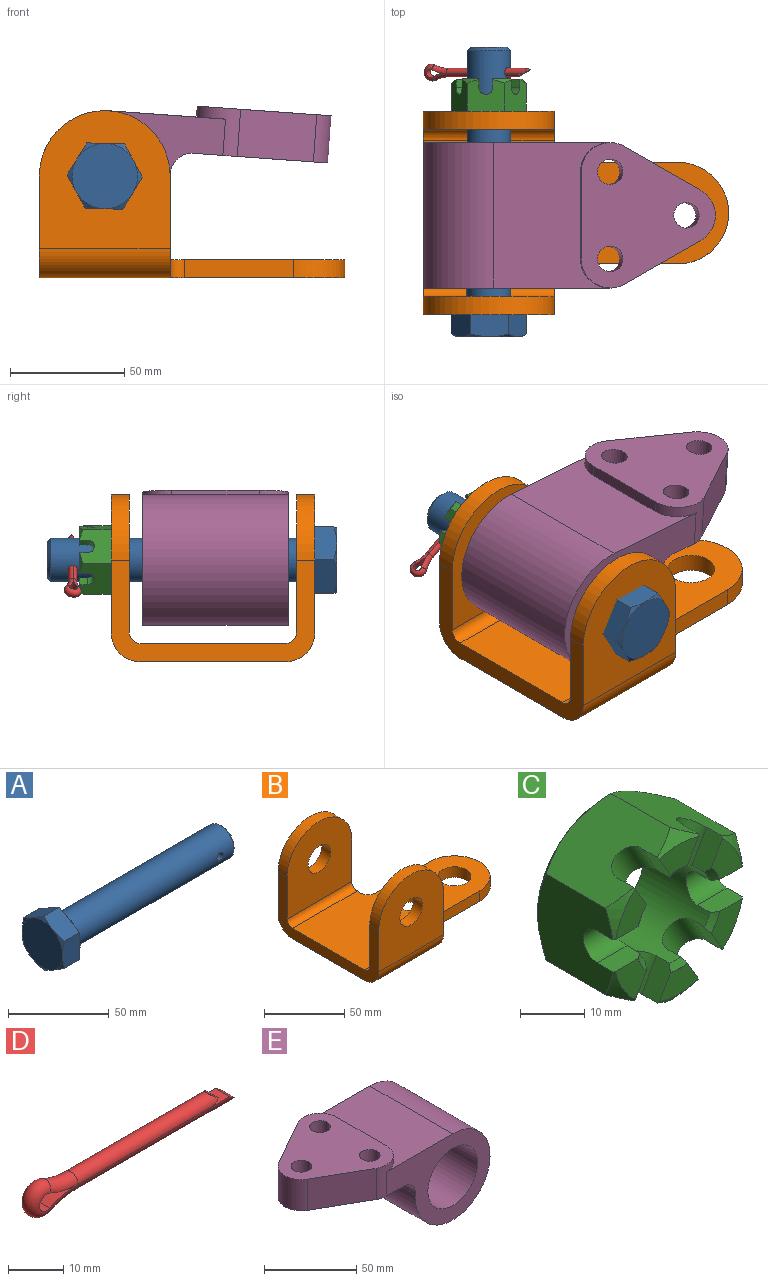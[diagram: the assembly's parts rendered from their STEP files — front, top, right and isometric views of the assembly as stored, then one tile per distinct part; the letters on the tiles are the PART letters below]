
ASSEMBLY  parts=5 mates=4
PART A: 26 faces, bbox 126.6x33x33 mm
  f0: plane 28.58x28.58mm, normal (1,0,0), area 325.1mm2, adj f10,f24
  f1: cylinder r=9.53mm len=112.28mm, axis (-1,0,0), area 6683.8mm2, adj f2,f24,f25
  f2: cone r=8.01mm half-angle=45deg, axis (-1,0,0), area 117.9mm2, adj f1,f3
  f3: plane 16.03x16.03mm, normal (1,0,0), area 201.7mm2, adj f2
  f4: plane 12.37x7.14mm, normal (1,0,0), area 11mm2, adj f10,f18,f23
  f5: plane 14.29x4.12mm, normal (1,0,0), area 11mm2, adj f10,f22,f23
  f6: plane 12.37x7.14mm, normal (1,0,0), area 11mm2, adj f10,f21,f22
  f7: plane 12.37x7.14mm, normal (1,0,0), area 11mm2, adj f10,f20,f21
  f8: plane 14.29x4.12mm, normal (1,0,0), area 11mm2, adj f10,f19,f20
  f9: plane 12.37x7.14mm, normal (1,0,0), area 11mm2, adj f10,f18,f19
  f10: cylinder r=14.29mm len=28.58mm, axis (-1,0,0), area 34.2mm2, adj f0,f4,f5,f6,f7,f8,f9
  f11: plane 28.58x28.58mm, normal (-1,0,0), area 641.3mm2, adj f12,f13,f14,f15,f16,f17
  f12: cone r=14.29mm half-angle=60deg, axis (1,0,0), area 12.7mm2, adj f11,f22,f23
  f13: cone r=14.29mm half-angle=60deg, axis (1,0,0), area 12.7mm2, adj f11,f21,f22
  f14: cone r=14.29mm half-angle=60deg, axis (1,0,0), area 12.7mm2, adj f11,f20,f21
  f15: cone r=14.29mm half-angle=60deg, axis (1,0,0), area 12.7mm2, adj f11,f19,f20
  f16: cone r=14.29mm half-angle=60deg, axis (1,0,0), area 12.7mm2, adj f11,f18,f23
  f17: cone r=14.29mm half-angle=60deg, axis (1,0,0), area 12.7mm2, adj f11,f18,f19
  f18: plane 16.51x11.89mm, normal (0,1,0), area 188.9mm2, adj f4,f9,f16,f17,f19,f23
  f19: plane 14.29x11.89mm, normal (0,0.5,-0.87), area 188.9mm2, adj f8,f9,f15,f17,f18,f20
  f20: plane 14.29x11.89mm, normal (0,-0.5,-0.87), area 188.9mm2, adj f7,f8,f14,f15,f19,f21
  f21: plane 16.51x11.89mm, normal (0,-1,0), area 188.9mm2, adj f6,f7,f13,f14,f20,f22
  f22: plane 14.29x11.89mm, normal (0,-0.5,0.87), area 188.9mm2, adj f5,f6,f12,f13,f21,f23
  f23: plane 14.29x11.89mm, normal (0,0.5,0.87), area 188.9mm2, adj f4,f5,f12,f16,f18,f22
  f24: torus R=10.03mm, axis (1,0,0), area 48.7mm2, adj f0,f1
  f25: cylinder r=2.38mm len=19.05mm, axis (0,-1,0), area 285mm2, adj f1
PART B: 24 faces, bbox 133.4x88.9x73 mm
  f0: plane 60.33x57.15mm, normal (0,-1,0), area 2787.8mm2, adj f5,f9,f10,f12,f22
  f1: plane 133.35x63.5mm, normal (0,0,1), area 6151.6mm2, adj f5,f8,f9,f13,f14,f15,f16,f17
  f2: plane 60.33x57.15mm, normal (0,-1,0), area 2787.8mm2, adj f5,f7,f8,f11,f20
  f3: plane 60.33x57.15mm, normal (0,1,0), area 2787.8mm2, adj f5,f9,f10,f12,f21
  f4: plane 60.33x57.15mm, normal (0,1,0), area 2787.8mm2, adj f5,f7,f8,f11,f23
  f5: plane 88.9x44.45mm, normal (-1,0,0), area 1225.8mm2, adj f0,f1,f2,f3,f4,f6,f7,f10
  f6: plane 133.35x63.5mm, normal (0,0,-1), area 6151.6mm2, adj f5,f8,f9,f13,f14,f15,f16,f17
  f7: cylinder r=28.57mm len=57.15mm, axis (0,-1,0), area 712.6mm2, adj f2,f4,f5,f8
  f8: plane 44.45x15.88mm, normal (1,0,0), area 386.1mm2, adj f1,f2,f4,f6,f7,f14,f20,f23
  f9: plane 44.45x15.88mm, normal (1,0,0), area 386.1mm2, adj f0,f1,f3,f6,f10,f18,f21,f22
  f10: cylinder r=28.57mm len=57.15mm, axis (0,-1,0), area 712.6mm2, adj f0,f3,f5,f9
  f11: cylinder r=9.92mm len=19.85mm, axis (0,-1,0), area 494.9mm2, adj f2,f4
  f12: cylinder r=9.92mm len=19.85mm, axis (0,-1,0), area 494.9mm2, adj f0,f3
  f13: cylinder r=10.33mm len=20.65mm, axis (0,0,1), area 514.9mm2, adj f1,f6
  f14: cylinder r=6.35mm len=7.94mm, axis (0,0,1), area 79.2mm2, adj f1,f6,f8,f15
  f15: plane 47.63x7.94mm, normal (0,1,0), area 378mm2, adj f1,f6,f14,f16
  f16: cylinder r=22.23mm len=44.45mm, axis (0,0,1), area 554.2mm2, adj f1,f6,f15,f19
  f17: cylinder r=10.33mm len=20.65mm, axis (0,0,1), area 514.9mm2, adj f1,f6
  f18: cylinder r=6.35mm len=7.94mm, axis (0,0,1), area 79.2mm2, adj f1,f6,f9,f19
  f19: plane 47.63x7.94mm, normal (0,-1,0), area 378mm2, adj f1,f6,f16,f18
  f20: cylinder r=4.76mm len=57.15mm, axis (1,0,0), area 427.5mm2, adj f1,f2,f5,f8
  f21: cylinder r=4.76mm len=57.15mm, axis (1,0,0), area 427.5mm2, adj f1,f3,f5,f9
  f22: cylinder r=12.7mm len=57.15mm, axis (-1,0,0), area 1140.1mm2, adj f0,f5,f6,f9
  f23: cylinder r=12.7mm len=57.15mm, axis (-1,0,0), area 1140.1mm2, adj f4,f5,f6,f8
PART C: 64 faces, bbox 33x16.9x33 mm
  f0: cylinder r=8.33mm len=16.67mm, axis (0,-1,0), area 599.6mm2, adj f8,f9,f10,f11,f12,f13,f14,f15
  f1: plane 28.58x28.58mm, normal (0,1,0), area 356.3mm2, adj f32,f33,f34,f35,f36,f37,f51
  f2: plane 8.68x4.95mm, normal (0,-1,0), area 30mm2, adj f12,f16,f41,f48
  f3: plane 7.52x6.81mm, normal (0,-1,0), area 30mm2, adj f9,f13,f43,f49
  f4: plane 7.52x6.81mm, normal (0,-1,0), area 30mm2, adj f8,f18,f39,f44
  f5: plane 7.52x6.81mm, normal (0,-1,0), area 30mm2, adj f11,f15,f42,f46
  f6: plane 7.52x6.81mm, normal (0,-1,0), area 30mm2, adj f10,f17,f40,f47
  f7: plane 8.68x4.95mm, normal (0,-1,0), area 30mm2, adj f14,f19,f38,f45
  f8: plane 6.56x3.71mm, normal (0,0,-1), area 23.4mm2, adj f0,f4,f22,f26,f39,f44,f62,f63
  f9: plane 6.56x3.71mm, normal (0,0,1), area 23.4mm2, adj f0,f3,f22,f26,f43,f49,f52,f53
  f10: plane 6.56x3.71mm, normal (0,0,1), area 23.4mm2, adj f0,f6,f25,f27,f40,f47,f56,f57
  f11: plane 6.56x3.71mm, normal (0,0,-1), area 23.4mm2, adj f0,f5,f25,f27,f42,f46,f58,f59
  f12: plane 5.69x3.71mm, normal (0.87,0,0.5), area 23.4mm2, adj f0,f2,f23,f28,f41,f48,f54,f55
  f13: plane 5.69x3.71mm, normal (-0.87,0,-0.5), area 23.4mm2, adj f0,f3,f23,f28,f43,f49,f52,f53
  f14: plane 5.69x3.71mm, normal (-0.87,0,-0.5), area 23.4mm2, adj f0,f7,f20,f29,f38,f45,f60,f61
  f15: plane 5.69x3.71mm, normal (0.87,0,0.5), area 23.4mm2, adj f0,f5,f20,f29,f42,f46,f58,f59
  f16: plane 5.69x3.71mm, normal (-0.87,0,0.5), area 23.4mm2, adj f0,f2,f24,f30,f41,f48,f54,f55
  f17: plane 5.69x3.71mm, normal (0.87,0,-0.5), area 23.4mm2, adj f0,f6,f24,f30,f40,f47,f56,f57
  f18: plane 5.69x3.71mm, normal (-0.87,0,0.5), area 23.4mm2, adj f0,f4,f21,f31,f39,f44,f62,f63
  f19: plane 5.69x3.71mm, normal (0.87,0,-0.5), area 23.4mm2, adj f0,f7,f21,f31,f38,f45,f60,f61
  f20: plane 16.62x14.29mm, normal (-0.5,0,0.87), area 220.6mm2, adj f14,f15,f21,f25,f29,f32,f33,f38
  f21: plane 16.62x14.29mm, normal (0.5,0,0.87), area 220.6mm2, adj f18,f19,f20,f22,f31,f33,f34,f38
  f22: plane 16.63x16.51mm, normal (1,0,0), area 220.6mm2, adj f8,f9,f21,f23,f26,f34,f35,f39
  f23: plane 16.62x14.29mm, normal (0.5,0,-0.87), area 220.6mm2, adj f12,f13,f22,f24,f28,f35,f36,f41
  f24: plane 16.62x14.29mm, normal (-0.5,0,-0.87), area 220.6mm2, adj f16,f17,f23,f25,f30,f36,f37,f40
  f25: plane 16.63x16.51mm, normal (-1,0,0), area 220.6mm2, adj f10,f11,f20,f24,f27,f32,f37,f40
  f26: cylinder r=3.05mm len=6.53mm, axis (1,0,0), area 59.8mm2, adj f0,f8,f9,f22
  f27: cylinder r=3.05mm len=6.53mm, axis (1,0,0), area 59.8mm2, adj f0,f10,f11,f25
  f28: cylinder r=3.05mm len=8.7mm, axis (-0.5,0,0.87), area 59.8mm2, adj f0,f12,f13,f23
  f29: cylinder r=3.05mm len=8.7mm, axis (-0.5,0,0.87), area 59.8mm2, adj f0,f14,f15,f20
  f30: cylinder r=3.05mm len=8.7mm, axis (0.5,0,0.87), area 59.8mm2, adj f0,f16,f17,f24
  f31: cylinder r=3.05mm len=8.7mm, axis (0.5,0,0.87), area 59.8mm2, adj f0,f18,f19,f21
  f32: cone r=14.29mm half-angle=49.2deg, axis (0,-1,0), area 14.5mm2, adj f1,f20,f25
  f33: cone r=14.29mm half-angle=49.2deg, axis (0,-1,0), area 14.5mm2, adj f1,f20,f21
  f34: cone r=14.29mm half-angle=49.2deg, axis (0,-1,0), area 14.5mm2, adj f1,f21,f22
  f35: cone r=14.29mm half-angle=49.2deg, axis (0,-1,0), area 14.5mm2, adj f1,f22,f23
  f36: cone r=14.29mm half-angle=49.2deg, axis (0,-1,0), area 14.5mm2, adj f1,f23,f24
  f37: cone r=14.29mm half-angle=49.2deg, axis (0,-1,0), area 14.5mm2, adj f1,f24,f25
  f38: cone r=14.29mm half-angle=49.2deg, axis (0,1,0), area 13.6mm2, adj f7,f14,f19,f20,f21
  f39: cone r=14.29mm half-angle=49.2deg, axis (0,1,0), area 13.6mm2, adj f4,f8,f18,f21,f22
  f40: cone r=14.29mm half-angle=49.2deg, axis (0,1,0), area 13.6mm2, adj f6,f10,f17,f24,f25
  f41: cone r=14.29mm half-angle=49.2deg, axis (0,1,0), area 13.6mm2, adj f2,f12,f16,f23,f24
  f42: cone r=14.29mm half-angle=49.2deg, axis (0,1,0), area 13.6mm2, adj f5,f11,f15,f20,f25
  f43: cone r=14.29mm half-angle=49.2deg, axis (0,1,0), area 13.6mm2, adj f3,f9,f13,f22,f23
  f44: cone r=8.21mm half-angle=55deg, axis (0,-1,0), area 0.1mm2, adj f4,f8,f18,f63
  f45: cone r=8.21mm half-angle=55deg, axis (0,-1,0), area 0.1mm2, adj f7,f14,f19,f60
  f46: cone r=8.21mm half-angle=55deg, axis (0,-1,0), area 0.1mm2, adj f5,f11,f15,f58
  f47: cone r=8.21mm half-angle=55deg, axis (0,-1,0), area 0.1mm2, adj f6,f10,f17,f56
  f48: cone r=8.21mm half-angle=55deg, axis (0,-1,0), area 0.1mm2, adj f2,f12,f16,f54
  f49: cone r=8.21mm half-angle=55deg, axis (0,-1,0), area 0.1mm2, adj f3,f9,f13,f52
  f50: cone r=9.53mm half-angle=55deg, axis (0,1,0), area 81.6mm2, adj f0,f51
  f51: cylinder r=9.53mm len=19.05mm, axis (0,-1,0), area 1.5mm2, adj f1,f50
  f52: cone r=9.53mm half-angle=55deg, axis (0,1,0), area 0.1mm2, adj f9,f13,f49,f53
  f53: cone r=8.33mm half-angle=55deg, axis (0,-1,0), area 4.5mm2, adj f0,f9,f13,f52
  f54: cone r=9.53mm half-angle=55deg, axis (0,1,0), area 0.1mm2, adj f12,f16,f48,f55
  f55: cone r=8.33mm half-angle=55deg, axis (0,-1,0), area 4.5mm2, adj f0,f12,f16,f54
  f56: cone r=9.53mm half-angle=55deg, axis (0,1,0), area 0.1mm2, adj f10,f17,f47,f57
  f57: cone r=8.33mm half-angle=55deg, axis (0,-1,0), area 4.5mm2, adj f0,f10,f17,f56
  f58: cone r=9.53mm half-angle=55deg, axis (0,1,0), area 0.1mm2, adj f11,f15,f46,f59
  f59: cone r=8.33mm half-angle=55deg, axis (0,-1,0), area 4.5mm2, adj f0,f11,f15,f58
  f60: cone r=9.53mm half-angle=55deg, axis (0,1,0), area 0.1mm2, adj f14,f19,f45,f61
  f61: cone r=8.33mm half-angle=55deg, axis (0,-1,0), area 4.5mm2, adj f0,f14,f19,f60
  f62: cone r=8.33mm half-angle=55deg, axis (0,-1,0), area 4.5mm2, adj f0,f8,f18,f63
  f63: cone r=9.53mm half-angle=55deg, axis (0,1,0), area 0.1mm2, adj f8,f18,f44,f62
PART D: 14 faces, bbox 52x3.7x8 mm
  f0: plane 38.67x3.7mm, normal (0,0,1), area 143.1mm2, adj f1,f2,f13
  f1: cylinder r=1.85mm len=40mm, axis (1,0,0), area 227.7mm2, adj f0,f3,f12,f13
  f2: cylinder r=16.37mm len=7.19mm, axis (0,1,0), area 27.5mm2, adj f0,f3,f4
  f3: torus R=16.37mm, axis (0,1,0), area 40.1mm2, adj f1,f2,f5
  f4: cylinder r=1.85mm len=3.7mm, axis (0,-1,0), area 27.8mm2, adj f2,f5,f6
  f5: torus R=1.85mm, axis (0,-1,0), area 71.2mm2, adj f3,f4,f7
  f6: cylinder r=16.37mm len=7.19mm, axis (0,1,0), area 27.5mm2, adj f4,f7,f9
  f7: torus R=16.37mm, axis (0,1,0), area 40.1mm2, adj f5,f6,f8
  f8: cylinder r=1.85mm len=36mm, axis (1,0,0), area 204.5mm2, adj f7,f9,f10,f11
  f9: plane 34.67x3.7mm, normal (0,0,-1), area 128.3mm2, adj f6,f8,f10
  f10: plane 3.7x1.33mm, normal (0.57,0,-0.82), area 5.7mm2, adj f8,f9,f11
  f11: plane 3.2x1.31mm, normal (0.58,0,0.82), area 3.6mm2, adj f8,f10
  f12: plane 3.2x1.31mm, normal (0.58,0,-0.82), area 3.6mm2, adj f1,f13
  f13: plane 3.7x1.33mm, normal (0.57,0,0.82), area 5.7mm2, adj f0,f1,f12
PART E: 17 faces, bbox 125.4x63.5x61.9 mm
  f0: plane 63.5x58.88mm, normal (0,0,-1), area 2387.5mm2, adj f1,f2,f4,f9,f10,f11,f12,f13
  f1: plane 79.38x57.15mm, normal (0,1,0), area 1971.2mm2, adj f0,f4,f5,f6,f7,f12
  f2: plane 79.38x57.15mm, normal (0,-1,0), area 1971.2mm2, adj f0,f4,f5,f6,f7,f9
  f3: plane 38.1x4.78mm, normal (1,0,0), area 181.9mm2, adj f6,f8,f9,f12
  f4: cylinder r=9.53mm len=63.5mm, axis (0,1,0), area 1000.5mm2, adj f0,f1,f2,f5
  f5: cylinder r=28.57mm len=63.5mm, axis (0,1,0), area 8702.1mm2, adj f1,f2,f4,f6
  f6: plane 63.5x50.8mm, normal (0,0,1), area 2488.6mm2, adj f1,f2,f3,f5,f9,f12
  f7: cylinder r=19.05mm len=63.5mm, axis (0,1,0), area 7600.6mm2, adj f1,f2
  f8: plane 63.5x58.75mm, normal (0,0,1), area 2309.8mm2, adj f3,f9,f10,f11,f12,f13,f14,f15
  f9: cylinder r=12.7mm len=20.65mm, axis (0,0,1), area 231.4mm2, adj f0,f2,f3,f6,f8,f10
  f10: plane 33.35x20.65mm, normal (-0.5,-0.87,0), area 793.1mm2, adj f0,f8,f9,f11
  f11: cylinder r=12.7mm len=22.06mm, axis (0,0,1), area 551.7mm2, adj f0,f8,f10,f13
  f12: cylinder r=12.7mm len=20.65mm, axis (0,0,1), area 231.4mm2, adj f0,f1,f3,f6,f8,f13
  f13: plane 33.35x20.65mm, normal (-0.5,0.87,0), area 793.1mm2, adj f0,f8,f11,f12
  f14: cylinder r=5.56mm len=20.65mm, axis (0,0,1), area 721.7mm2, adj f0,f8
  f15: cylinder r=5.56mm len=20.65mm, axis (0,0,1), area 721.7mm2, adj f0,f8
  f16: cylinder r=5.56mm len=20.65mm, axis (0,0,1), area 721.7mm2, adj f0,f8
PLACE A rot(axis=(-0.24,-0.24,0.94),93.5deg) t=(28.57,-54.14,44.45)mm
PLACE B at identity fixed
PLACE C rot(axis=(0.21,0,0.98),180deg) t=(28.58,58.49,44.45)mm
PLACE D rot(axis=(0.95,-0.2,0.24),103.4deg) t=(3.86,61.31,31.03)mm
PLACE E rot(axis=(-0.04,0,-1),180deg) t=(28.58,-32.86,44.45)mm
MATE cylindrical C.f0 <-> B.f7  axis (0,-1,0) through (28.58,41.6,44.45)mm
MATE revolute E.f5 <-> B.f7  axis (0,-1,0) through (28.58,-32.86,44.45)mm
MATE revolute D.f1 <-> A.f25  axis (0.88,0,0.48) through (28.58,61.31,44.45)mm
MATE cylindrical A.f1 <-> B.f7  axis (0,-1,0) through (28.58,-41.36,44.45)mm
